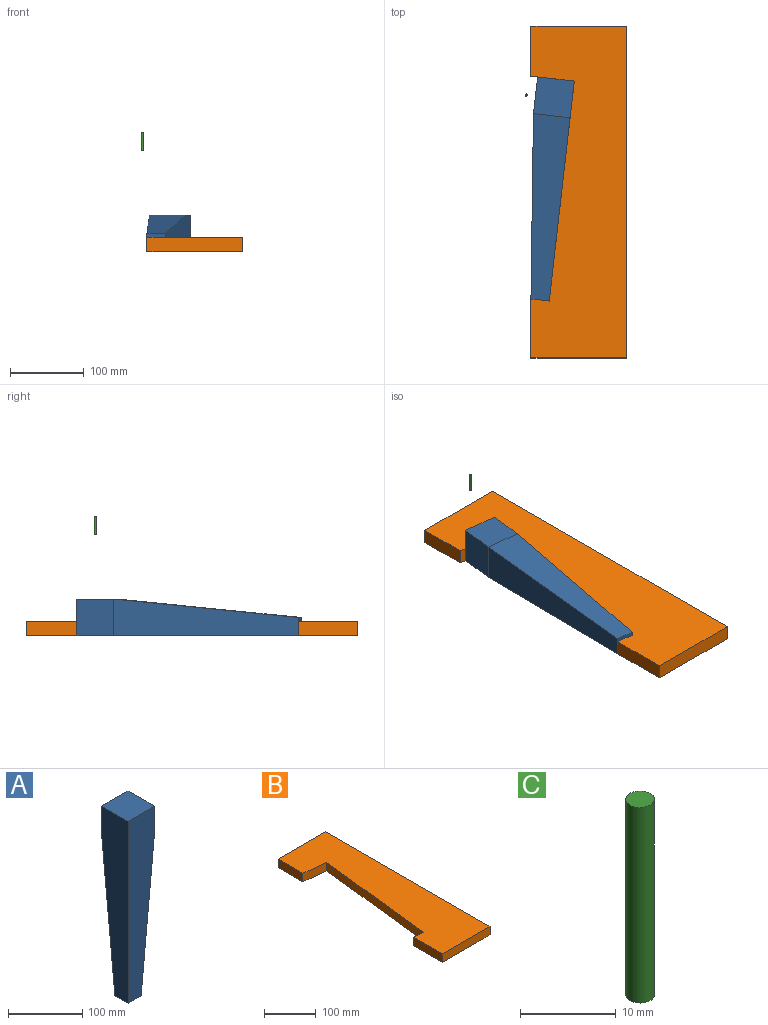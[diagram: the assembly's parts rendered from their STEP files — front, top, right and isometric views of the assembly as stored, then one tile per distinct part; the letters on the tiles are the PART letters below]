
ASSEMBLY  parts=3 mates=1
PART A: 8 faces, bbox 50x50x300 mm
  f0: plane 25x25mm, normal (0,0,-1), area 625mm2, adj f3,f4,f6,f7
  f1: plane 50x50mm, normal (0,1,0), area 2500mm2, adj f2,f3,f5,f7
  f2: plane 50x50mm, normal (1,0,0), area 2500mm2, adj f1,f4,f5,f6
  f3: plane 300x50mm, normal (-1,0,0), area 11875mm2, adj f0,f1,f4,f5,f7
  f4: plane 300x50mm, normal (0,-1,0), area 11875mm2, adj f0,f2,f3,f5,f6
  f5: plane 50x50mm, normal (0,0,1), area 2500mm2, adj f1,f2,f3,f4
  f6: plane 250x50mm, normal (1,0,-0.1), area 9421.8mm2, adj f0,f2,f4,f7
  f7: plane 250x50mm, normal (0,1,-0.1), area 9421.8mm2, adj f0,f1,f3,f6
PART B: 10 faces, bbox 130x450x20 mm
  f0: plane 24.84x20mm, normal (0.11,0.99,0), area 500mm2, adj f1,f7,f8,f9
  f1: plane 80x20mm, normal (-1,0,0), area 1600mm2, adj f0,f2,f8,f9
  f2: plane 130x20mm, normal (0,-1,0), area 2600mm2, adj f1,f3,f8,f9
  f3: plane 450x20mm, normal (1,0,0), area 9000mm2, adj f2,f4,f8,f9
  f4: plane 130x20mm, normal (0,1,0), area 2600mm2, adj f3,f5,f8,f9
  f5: plane 68.07x20mm, normal (-1,0,0), area 1361.4mm2, adj f4,f6,f8,f9
  f6: plane 58.71x20mm, normal (-0.11,-0.99,0), area 1181.8mm2, adj f5,f7,f8,f9
  f7: plane 298.08x33.87mm, normal (-0.99,0.11,0), area 6000mm2, adj f0,f6,f8,f9
  f8: plane 450x130mm, normal (0,0,1), area 45886.4mm2, adj f0,f1,f2,f3,f4,f5,f6,f7
  f9: plane 450x130mm, normal (0,0,-1), area 45886.4mm2, adj f0,f1,f2,f3,f4,f5,f6,f7
PART C: 3 faces, bbox 3x3x25 mm
  f0: cylinder r=1.5mm len=25mm, axis (0,0,-1), area 235.6mm2, adj f1,f2
  f1: plane 3x3mm, normal (0,0,1), area 7.1mm2, adj f0
  f2: plane 3x3mm, normal (0,0,-1), area 7.1mm2, adj f0
PLACE A rot(axis=(0.04,0.71,0.71),175.4deg) t=(7.9,-151.86,0)mm
PLACE B at identity fixed
PLACE C t=(-148.31,2.05,-162.5)mm
MATE fastened A.f5 <-> B.f6  axis (0.11,0.99,0) through (41.78,146.22,0)mm
